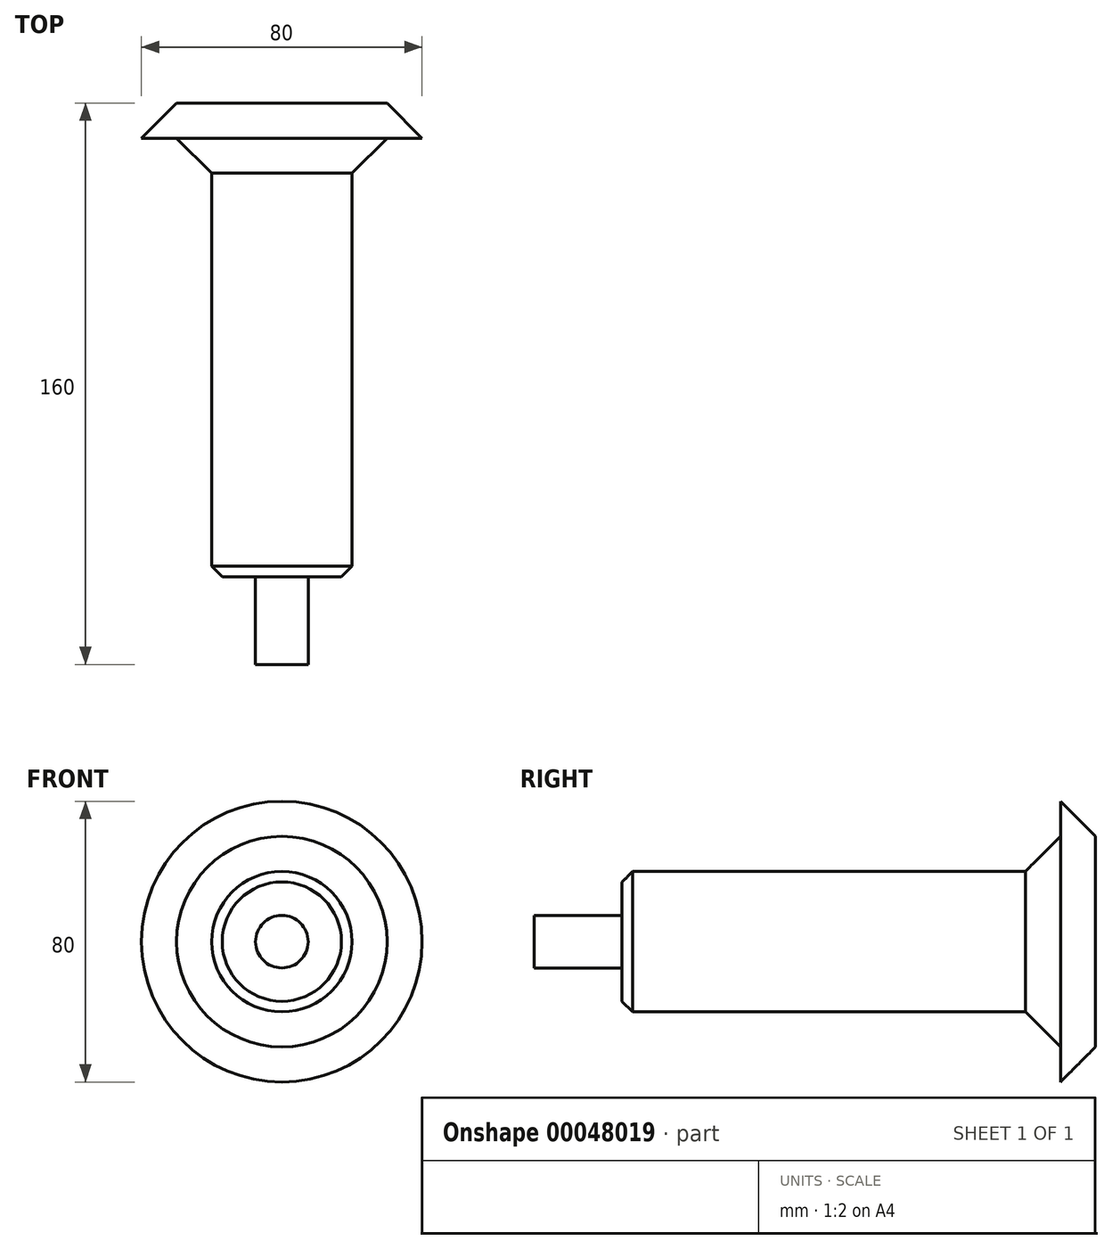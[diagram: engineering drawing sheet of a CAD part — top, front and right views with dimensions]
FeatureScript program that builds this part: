
annotation { "Feature Type Name" : "Feature", "Feature Type Description" : "" }
export const myFeature = defineFeature(function(context is Context, id is Id, definition is map)
    precondition{}
    {
        {
            var Q0;
            Q0=qCreatedBy(makeId("Right.planeOp"),FACE);
            var sketch = newSketch(context, id + "F0", { "sketchPlane" : qUnion([Q0])});
            skLineSegment(sketch, "E0", {"start": v(0, 0) * mm, "end": v(0, 40) * mm});
            skLineSegment(sketch, "E1", {"start": v(0, 40) * mm, "end": v(-10, 40) * mm});
            skLineSegment(sketch, "E2", {"start": v(-10, 40) * mm, "end": v(-10, 20) * mm});
            skLineSegment(sketch, "E3", {"start": v(-10, 20) * mm, "end": v(-135, 20) * mm});
            skLineSegment(sketch, "E4", {"start": v(-135, 20) * mm, "end": v(-135, 7.5) * mm});
            skLineSegment(sketch, "E5", {"start": v(-135, 7.5) * mm, "end": v(-160, 7.5) * mm});
            skLineSegment(sketch, "E6", {"start": v(-160, 7.5) * mm, "end": v(-160, 0) * mm});
            skLineSegment(sketch, "E7", {"start": v(-160, 0) * mm, "end": v(0, 0) * mm});
            skLineSegment(sketch, "E8", {"start": v(-81.52, 0) * mm, "end": v(13.94, 0) * mm, "construction": true});
            skSolve(sketch);
        }
        {
            var Q0;
            Q0 = qSketchRegion(id + "F0", true);
            var Q1;
            Q1=sQuery(id+"F0.wireOp",EDGE,"E8");
            revolve(context, id + "F1", {"entities" : qUnion([Q0]), "axis" : qUnion([Q1]), "revolveType" : RevolveType.FULL});
        }
        {
            var Q0;
            Q0=makeQuery(id+"F1.opRevolve","SWEPT_EDGE",EDGE,{"disambiguationData":[OSD([sQuery(id+"F0.wireOp",EDGE,"E3"),sQuery(id+"F0.wireOp",EDGE,"E4")])]});
            chamfer(context, id + "F2", {"entities" : qUnion([Q0]), "width" : 3 * mm, "tangentPropagation" : true});
        }
        {
            var Q0;
            Q0=makeQuery(id+"F1.opRevolve","SWEPT_EDGE",EDGE,{"disambiguationData":[OSD([sQuery(id+"F0.wireOp",EDGE,"E2"),sQuery(id+"F0.wireOp",EDGE,"E3")])]});
            chamfer(context, id + "F3", {"entities" : qUnion([Q0]), "width" : 10 * mm, "tangentPropagation" : true});
        }
        {
            var Q0;
            Q0=makeQuery(id+"F1.opRevolve","SWEPT_EDGE",EDGE,{"disambiguationData":[OSD([sQuery(id+"F0.wireOp",EDGE,"E0"),sQuery(id+"F0.wireOp",EDGE,"E1")])]});
            chamfer(context, id + "F4", {"entities" : qUnion([Q0]), "width" : 10 * mm, "tangentPropagation" : true});
        }
    });
